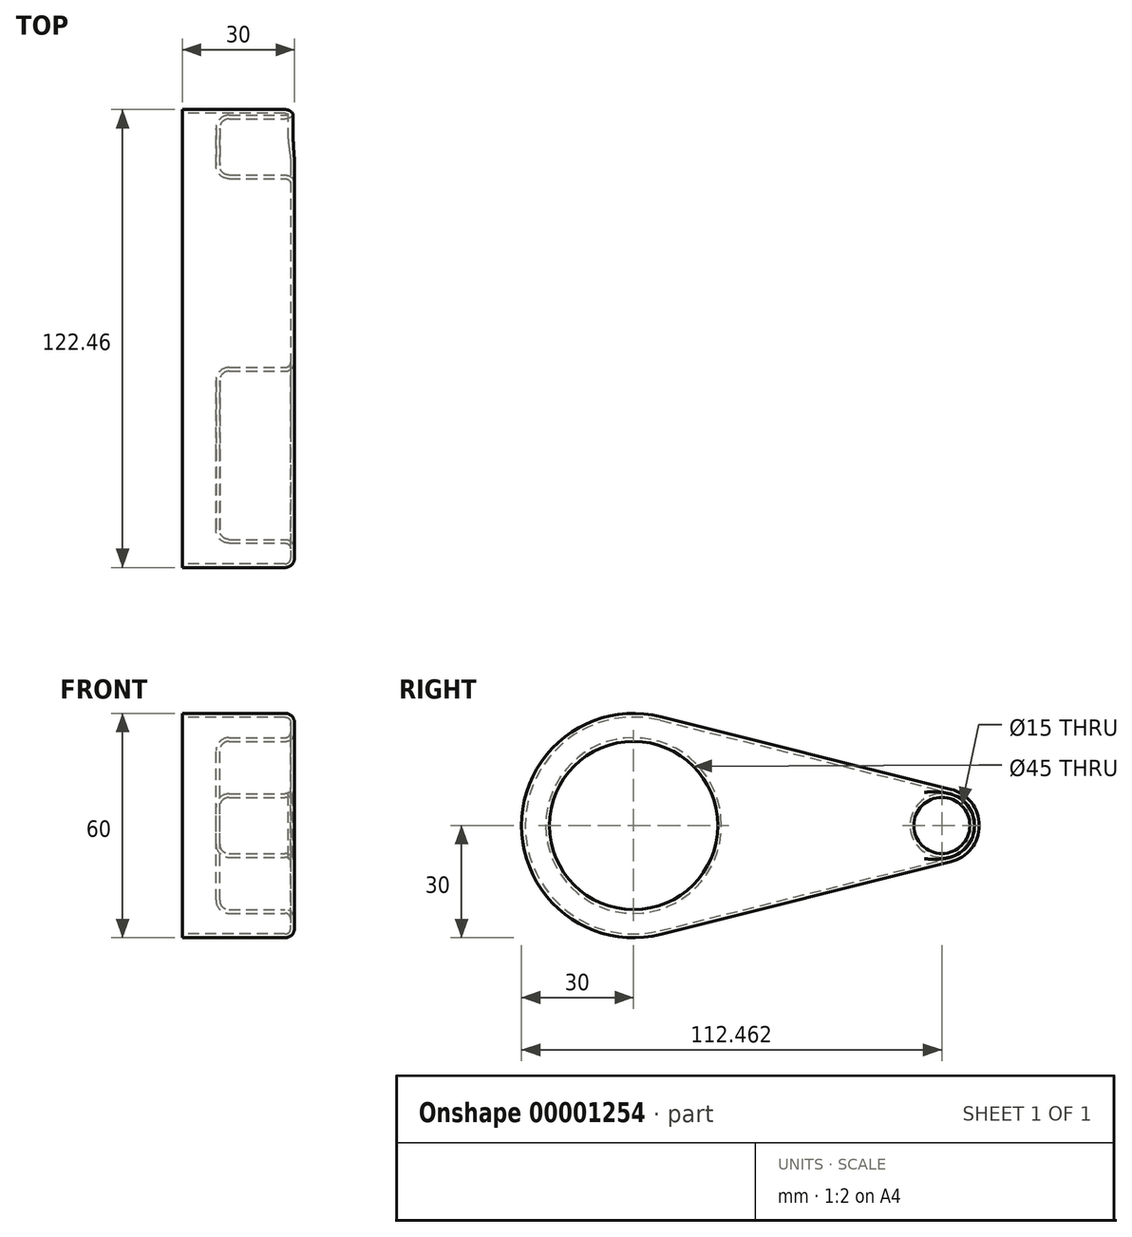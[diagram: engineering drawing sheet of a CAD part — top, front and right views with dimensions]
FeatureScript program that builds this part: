
annotation { "Feature Type Name" : "Feature", "Feature Type Description" : "" }
export const myFeature = defineFeature(function(context is Context, id is Id, definition is map)
    precondition{}
    {
        {
            var Q0;
            Q0=qCreatedBy(makeId("Right.planeOp"),FACE);
            var sketch = newSketch(context, id + "F0", { "sketchPlane" : qUnion([Q0])});
            skCircle(sketch, "E0", {"center": v(0, 0) * mm, "radius": 30 * mm});
            skCircle(sketch, "E1", {"center": v(82.46, 0) * mm, "radius": 10 * mm});
            skLineSegment(sketch, "E2", {"start": v(7.28, 29.1) * mm, "end": v(84.89, 9.7) * mm});
            skLineSegment(sketch, "E3", {"start": v(7.28, -29.1) * mm, "end": v(84.89, -9.7) * mm});
            skSolve(sketch);
        }
        {
            var Q0;
            {var subQ0=sQuery(id+"F0.wireOp",EDGE,"E1");var subQ2=makeQuery(id+"F0.imprint","INTERSECT",VERTEX,{"derivedFrom":[subQ0,sQuery(id+"F0.wireOp",EDGE,"E2")]});Q0=makeQuery(id+"F0.imprint","IMPRINT",FACE,{"disambiguationData":[TD([[makeQuery(id+"F0.imprint","IMPRINT",EDGE,{"disambiguationData":[TD([[subQ2,-1.0]])],"derivedFrom":subQ0}),1.0]])]});}
            var Q1;
            {var subQ0=sQuery(id+"F0.wireOp",EDGE,"E0");var subQ2=makeQuery(id+"F0.imprint","INTERSECT",VERTEX,{"derivedFrom":[subQ0,sQuery(id+"F0.wireOp",EDGE,"E2")]});Q1=makeQuery(id+"F0.imprint","IMPRINT",FACE,{"disambiguationData":[TD([[makeQuery(id+"F0.imprint","IMPRINT",EDGE,{"disambiguationData":[TD([[subQ2,-1.0]])],"derivedFrom":subQ0}),1.0]])]});}
            var Q2;
            {var subQ1=sQuery(id+"F0.wireOp",EDGE,"E2");Q2=makeQuery(id+"F0.imprint","IMPRINT",FACE,{"disambiguationData":[TD([[makeQuery(id+"F0.imprint","IMPRINT",EDGE,{"derivedFrom":subQ1}),-1.0]])]});}
            extrude(context, id + "F1", {"entities" : qUnion([Q0, Q1, Q2]), "depth" : 30 * mm});
        }
        {
            var Q0;
            Q0=makeQuery(id+"F1.opExtrude","CAP_FACE",FACE,{"disambiguationData":[OSD([sQuery(id+"F0.wireOp",EDGE,"E0"),sQuery(id+"F0.wireOp",EDGE,"E1"),sQuery(id+"F0.wireOp",EDGE,"E2"),sQuery(id+"F0.wireOp",EDGE,"E3")])],"isStart":false});
            var sketch = newSketch(context, id + "F2", { "sketchPlane" : qUnion([Q0])});
            skCircle(sketch, "E4", {"center": v(0, 0) * mm, "radius": 22.5 * mm});
            skCircle(sketch, "E5", {"center": v(82.46, 0) * mm, "radius": 7.5 * mm});
            skArc(sketch, "E6.0.0", {"start": v(7.28, 29.1) * mm, "mid": v(-30, 0) * mm, "end": v(7.28, -29.1) * mm});
            skArc(sketch, "E6.0.2", {"start": v(7.28, 29.1) * mm, "mid": v(-30, 0) * mm, "end": v(7.28, -29.1) * mm});
            skArc(sketch, "E7.0.0", {"start": v(84.89, -9.7) * mm, "mid": v(92.46, 0) * mm, "end": v(84.89, 9.7) * mm});
            skLineSegment(sketch, "E7.0.1", {"start": v(7.28, 29.1) * mm, "end": v(84.89, 9.7) * mm});
            skLineSegment(sketch, "E7.0.3", {"start": v(7.28, -29.1) * mm, "end": v(84.89, -9.7) * mm});
            skCircle(sketch, "E8.0", {"center": v(0, 0) * mm, "radius": 30 * mm});
            skCircle(sketch, "E8.1", {"center": v(82.46, 0) * mm, "radius": 10 * mm});
            skSolve(sketch);
        }
        {
            var Q0;
            Q0=makeQuery(id+"F2.imprint","IMPRINT",FACE,{"disambiguationData":[TD([[makeQuery(id+"F2.imprint","IMPRINT",EDGE,{"derivedFrom":sQuery(id+"F2.wireOp",EDGE,"E4")}),1.0]])]});
            var Q1;
            Q1=makeQuery(id+"F2.imprint","IMPRINT",FACE,{"disambiguationData":[TD([[makeQuery(id+"F2.imprint","IMPRINT",EDGE,{"derivedFrom":sQuery(id+"F2.wireOp",EDGE,"E5")}),1.0]])]});
            extrude(context, id + "F3", {"entities" : qUnion([Q0, Q1]), "operationType" : NewBodyOperationType.REMOVE, "oppositeDirection" : true, "depth" : 20 * mm});
        }
        {
            var Q0;
            Q0=makeQuery(id+"F1.opExtrude","CAP_FACE",FACE,{"disambiguationData":[OSD([sQuery(id+"F0.wireOp",EDGE,"E0"),sQuery(id+"F0.wireOp",EDGE,"E1"),sQuery(id+"F0.wireOp",EDGE,"E2"),sQuery(id+"F0.wireOp",EDGE,"E3")])],"isStart":false});
            var Q1;
            Q1=makeQuery(id+"F3.boolean.opBoolean","COPY",EDGE,{"derivedFrom":makeQuery(id+"F3.opExtrude","CAP_EDGE",EDGE,{"disambiguationData":[OSD([sQuery(id+"F2.wireOp",EDGE,"E4")])],"isStart":false})});
            var Q2;
            Q2=makeQuery(id+"F3.boolean.opBoolean","COPY",EDGE,{"derivedFrom":makeQuery(id+"F3.opExtrude","CAP_EDGE",EDGE,{"disambiguationData":[OSD([sQuery(id+"F2.wireOp",EDGE,"E5")])],"isStart":false})});
            fillet(context, id + "F4", {"entities" : qUnion([Q0, Q1, Q2]), "radius" : 2.5 * mm, "tangentPropagation" : true, "allowEdgeOverflow" : false});
        }
        {
            var Q0;
            Q0=makeQuery(id+"F1.opExtrude","CAP_FACE",FACE,{"disambiguationData":[OSD([sQuery(id+"F0.wireOp",EDGE,"E0"),sQuery(id+"F0.wireOp",EDGE,"E1"),sQuery(id+"F0.wireOp",EDGE,"E2"),sQuery(id+"F0.wireOp",EDGE,"E3")])],"isStart":true});
            shell(context, id + "F5", {"entities" : qUnion([Q0]), "thickness" : 1 * mm});
        }
    });
